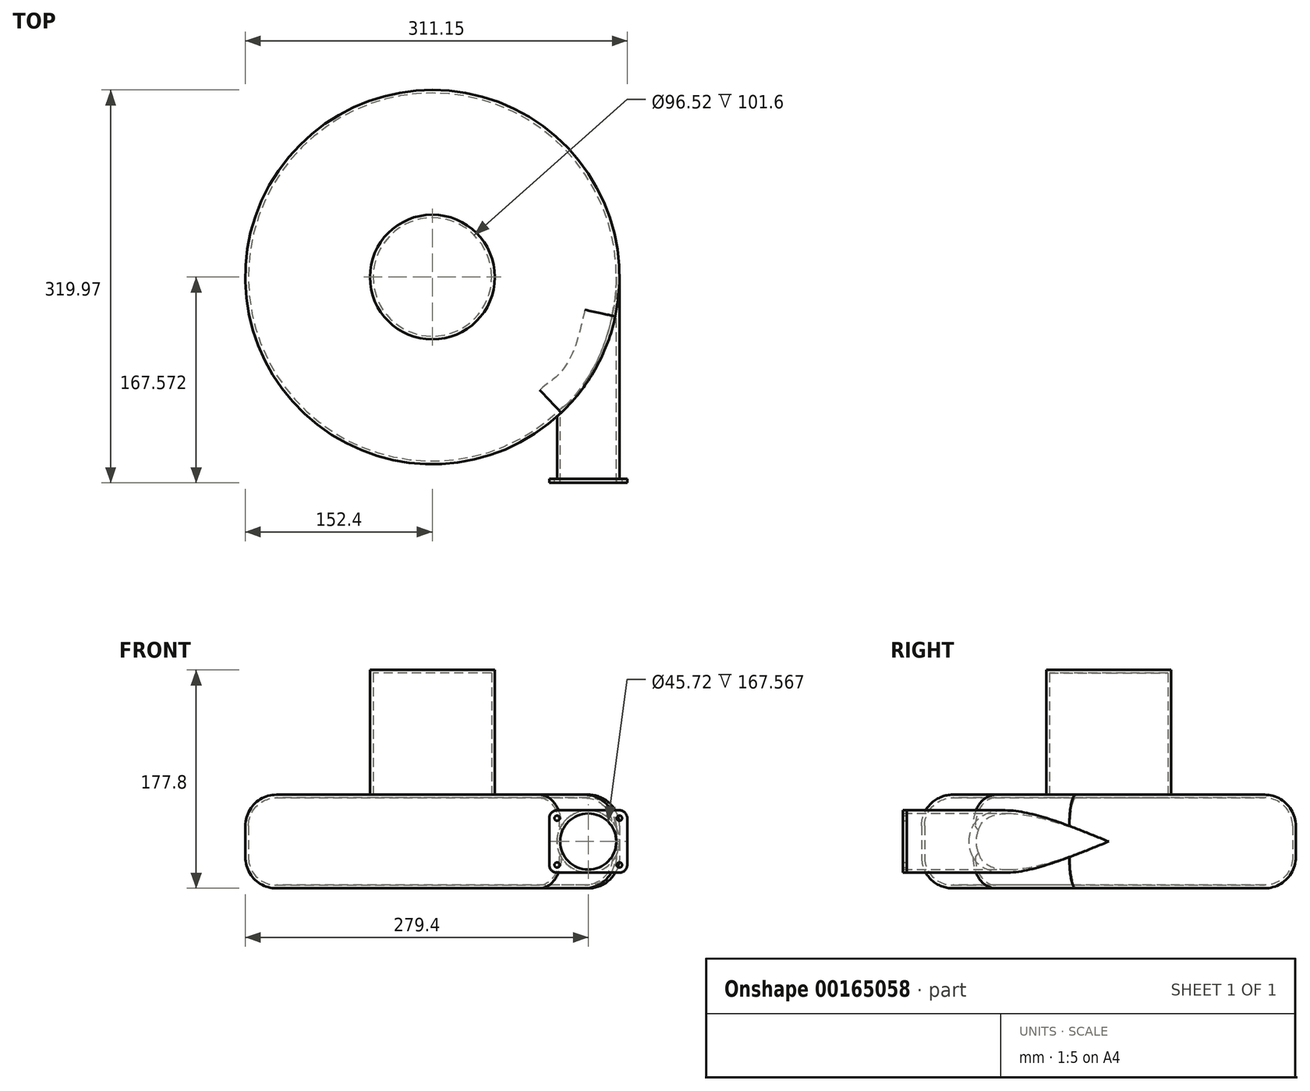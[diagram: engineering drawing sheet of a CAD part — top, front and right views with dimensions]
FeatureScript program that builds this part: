
annotation { "Feature Type Name" : "Feature", "Feature Type Description" : "" }
export const myFeature = defineFeature(function(context is Context, id is Id, definition is map)
    precondition{}
    {
        {
            var Q0;
            Q0=qCreatedBy(makeId("Top.planeOp"),FACE);
            var sketch = newSketch(context, id + "F0", { "sketchPlane" : qUnion([Q0])});
            skLineSegment(sketch, "E0.top", {"start": v(0, -50.8) * mm, "end": v(50.8, -50.8) * mm});
            skLineSegment(sketch, "E0.left", {"start": v(0, 0) * mm, "end": v(0, -50.8) * mm});
            skLineSegment(sketch, "E0.right", {"start": v(50.8, 113.6) * mm, "end": v(50.8, -50.8) * mm});
            skArc(sketch, "E1", {"start": v(50.8, 113.6) * mm, "mid": v(-240.72, 175.8) * mm, "end": v(0, 0) * mm});
            skSolve(sketch);
        }
        {
            var Q0;
            Q0=qSketchRegion(id+"F0",true);
            extrude(context, id + "F1", {"entities" : qUnion([Q0]), "depth" : 50.8 * mm});
        }
        {
            var Q0;
            Q0=makeQuery(id+"F1.opExtrude","CAP_FACE",FACE,{"disambiguationData":[OSD([sQuery(id+"F0.wireOp",EDGE,"E0.top"),sQuery(id+"F0.wireOp",EDGE,"E0.left"),sQuery(id+"F0.wireOp",EDGE,"E0.right"),sQuery(id+"F0.wireOp",EDGE,"E1")])],"isStart":false});
            var sketch = newSketch(context, id + "F2", { "sketchPlane" : qUnion([Q0])});
            skCircle(sketch, "E2", {"center": v(-101.6, 113.6) * mm, "radius": 152.4 * mm});
            skSolve(sketch);
        }
        {
            var Q0;
            Q0=qSketchRegion(id+"F2",true);
            extrude(context, id + "F3", {"entities" : qUnion([Q0]), "operationType" : NewBodyOperationType.ADD, "depth" : 12.7 * mm, "hasSecondDirection" : true, "secondDirectionOppositeDirection" : true, "secondDirectionDepth" : 63.5 * mm});
        }
        {
            var Q0;
            Q0=makeQuery(id+"F1.opExtrude","CAP_EDGE",EDGE,{"disambiguationData":[OSD([sQuery(id+"F0.wireOp",EDGE,"E0.left")])],"isStart":false});
            var Q1;
            Q1=makeQuery(id+"F1.opExtrude","CAP_EDGE",EDGE,{"disambiguationData":[OSD([sQuery(id+"F0.wireOp",EDGE,"E0.left")])],"isStart":true});
            var Q2;
            Q2=makeQuery(id+"F1.opExtrude","CAP_EDGE",EDGE,{"disambiguationData":[OSD([sQuery(id+"F0.wireOp",EDGE,"E0.right")])],"isStart":false});
            var Q3;
            Q3=makeQuery(id+"F1.opExtrude","CAP_EDGE",EDGE,{"disambiguationData":[OSD([sQuery(id+"F0.wireOp",EDGE,"E0.right")])],"isStart":true});
            fillet(context, id + "F4", {"entities" : qUnion([Q0, Q1, Q2, Q3]), "radius" : 25.4 * mm, "tangentPropagation" : true, "allowEdgeOverflow" : false});
        }
        {
            var Q0;
            Q0=makeQuery(id+"F3.opExtrude","CAP_EDGE",EDGE,{"disambiguationData":[OSD([sQuery(id+"F2.wireOp",EDGE,"E2")])],"isStart":false});
            var Q1;
            Q1=makeQuery(id+"F3.opExtrude","CAP_EDGE",EDGE,{"disambiguationData":[OSD([sQuery(id+"F2.wireOp",EDGE,"E2")])],"isStart":true});
            fillet(context, id + "F5", {"entities" : qUnion([Q0, Q1]), "radius" : 25.4 * mm, "tangentPropagation" : true, "allowEdgeOverflow" : false});
        }
        {
            var Q0;
            Q0=makeQuery(id+"F3.opExtrude","CAP_FACE",FACE,{"disambiguationData":[OSD([sQuery(id+"F2.wireOp",EDGE,"E2")])],"isStart":false});
            var sketch = newSketch(context, id + "F6", { "sketchPlane" : qUnion([Q0])});
            skCircle(sketch, "E3", {"center": v(-101.6, 113.6) * mm, "radius": 50.8 * mm});
            skSolve(sketch);
        }
        {
            var Q0;
            Q0=qSketchRegion(id+"F6",true);
            extrude(context, id + "F7", {"entities" : qUnion([Q0]), "operationType" : NewBodyOperationType.ADD, "depth" : 101.6 * mm});
        }
        {
            var Q0;
            Q0=makeQuery(id+"F1.opExtrude","SWEPT_FACE",FACE,{"disambiguationData":[OSD([sQuery(id+"F0.wireOp",EDGE,"E0.top")])]});
            shell(context, id + "F8", {"entities" : qUnion([Q0]), "thickness" : 2.54 * mm});
        }
        {
            var Q0;
            Q0=makeQuery(id+"F1.opExtrude","SWEPT_FACE",FACE,{"disambiguationData":[OSD([sQuery(id+"F0.wireOp",EDGE,"E0.top")])]});
            var sketch = newSketch(context, id + "F9", { "sketchPlane" : qUnion([Q0])});
            skLineSegment(sketch, "E4.bottom", {"start": v(57.15, 0) * mm, "end": v(-6.35, 0) * mm});
            skLineSegment(sketch, "E4.top", {"start": v(57.15, 50.8) * mm, "end": v(-6.35, 50.8) * mm});
            skLineSegment(sketch, "E4.left", {"start": v(57.15, 0) * mm, "end": v(57.15, 50.8) * mm});
            skLineSegment(sketch, "E4.right", {"start": v(-6.35, 0) * mm, "end": v(-6.35, 50.8) * mm});
            skPoint(sketch, "E4.middle", {"position": v(25.4, 25.4) * mm});
            skLineSegment(sketch, "E5.bottom", {"start": v(50.8, 44.45) * mm, "end": v(0, 44.45) * mm, "construction": true});
            skLineSegment(sketch, "E5.top", {"start": v(50.8, 6.35) * mm, "end": v(0, 6.35) * mm, "construction": true});
            skLineSegment(sketch, "E5.left", {"start": v(50.8, 44.45) * mm, "end": v(50.8, 6.35) * mm, "construction": true});
            skLineSegment(sketch, "E5.right", {"start": v(0, 44.45) * mm, "end": v(0, 6.35) * mm, "construction": true});
            skCircle(sketch, "E6", {"center": v(50.8, 44.45) * mm, "radius": 6.35 * mm, "construction": true});
            skCircle(sketch, "E7", {"center": v(0, 44.45) * mm, "radius": 2.15 * mm});
            skCircle(sketch, "E8", {"center": v(50.8, 44.45) * mm, "radius": 2.15 * mm});
            skCircle(sketch, "E9", {"center": v(50.8, 6.35) * mm, "radius": 2.15 * mm});
            skCircle(sketch, "E10", {"center": v(0, 6.35) * mm, "radius": 2.15 * mm});
            skCircle(sketch, "E11", {"center": v(25.4, 25.4) * mm, "radius": 22.86 * mm});
            skSolve(sketch);
        }
        {
            var Q0;
            Q0 = qSketchRegion(id + "F9", true);
            extrude(context, id + "F10", {"entities" : qUnion([Q0]), "operationType" : NewBodyOperationType.ADD, "depth" : 3.17 * mm});
        }
        {
            var Q0;
            Q0=makeQuery(id+"F10.opExtrude","SWEPT_EDGE",EDGE,{"disambiguationData":[OSD([sQuery(id+"F9.wireOp",EDGE,"E4.top"),sQuery(id+"F9.wireOp",EDGE,"E4.left")])]});
            var Q1;
            Q1=makeQuery(id+"F10.opExtrude","SWEPT_EDGE",EDGE,{"disambiguationData":[OSD([sQuery(id+"F9.wireOp",EDGE,"E4.bottom"),sQuery(id+"F9.wireOp",EDGE,"E4.left")])]});
            var Q2;
            Q2=makeQuery(id+"F10.opExtrude","SWEPT_EDGE",EDGE,{"disambiguationData":[OSD([sQuery(id+"F9.wireOp",EDGE,"E4.bottom"),sQuery(id+"F9.wireOp",EDGE,"E4.right")])]});
            var Q3;
            Q3=makeQuery(id+"F10.opExtrude","SWEPT_EDGE",EDGE,{"disambiguationData":[OSD([sQuery(id+"F9.wireOp",EDGE,"E4.top"),sQuery(id+"F9.wireOp",EDGE,"E4.right")])]});
            fillet(context, id + "F11", {"entities" : qUnion([Q0, Q1, Q2, Q3]), "radius" : 6.35 * mm, "tangentPropagation" : true, "allowEdgeOverflow" : false});
        }
    });
